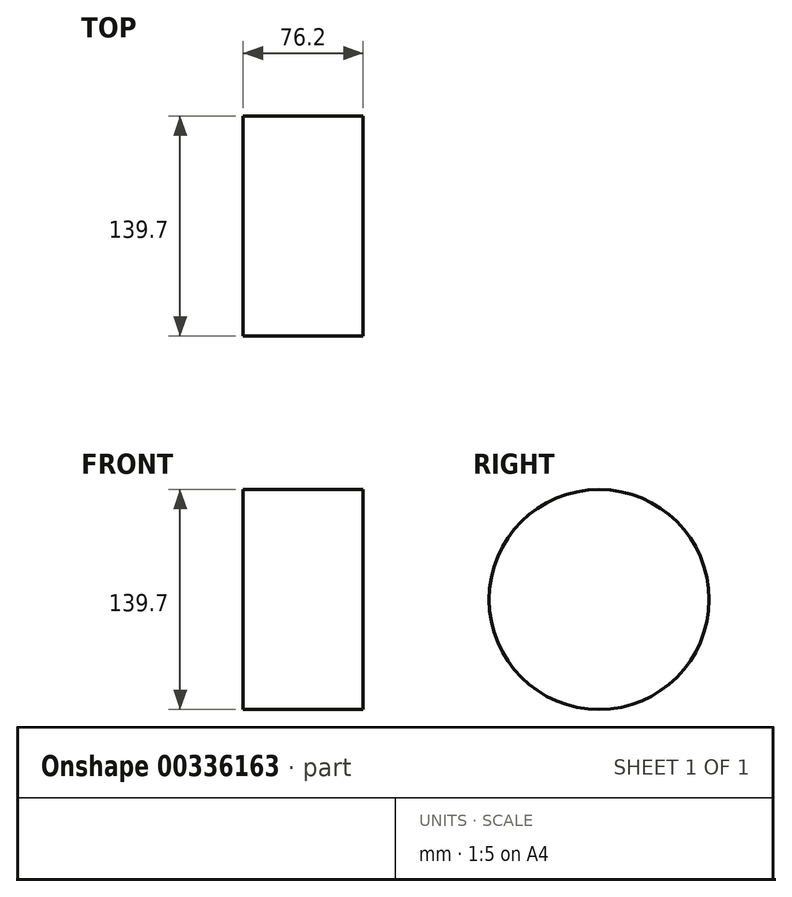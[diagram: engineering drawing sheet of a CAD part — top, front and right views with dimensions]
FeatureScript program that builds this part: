
annotation { "Feature Type Name" : "Feature", "Feature Type Description" : "" }
export const myFeature = defineFeature(function(context is Context, id is Id, definition is map)
    precondition{}
    {
        {
            var Q0;
            Q0=qCreatedBy(makeId("Right.planeOp"),FACE);
            var sketch = newSketch(context, id + "F0", { "sketchPlane" : qUnion([Q0])});
            skCircle(sketch, "E0", {"center": v(-66.47, 38.92) * mm, "radius": 69.85 * mm});
            skSolve(sketch);
        }
        {
            var Q0;
            Q0=makeQuery(id+"F0.imprint","IMPRINT",FACE,{"disambiguationData":[TD([[makeQuery(id+"F0.imprint","IMPRINT",EDGE,{"derivedFrom":sQuery(id+"F0.wireOp",EDGE,"E0")}),1.0]])]});
            extrude(context, id + "F1", {"entities" : qUnion([Q0]), "depth" : 76.2 * mm});
        }
    });
